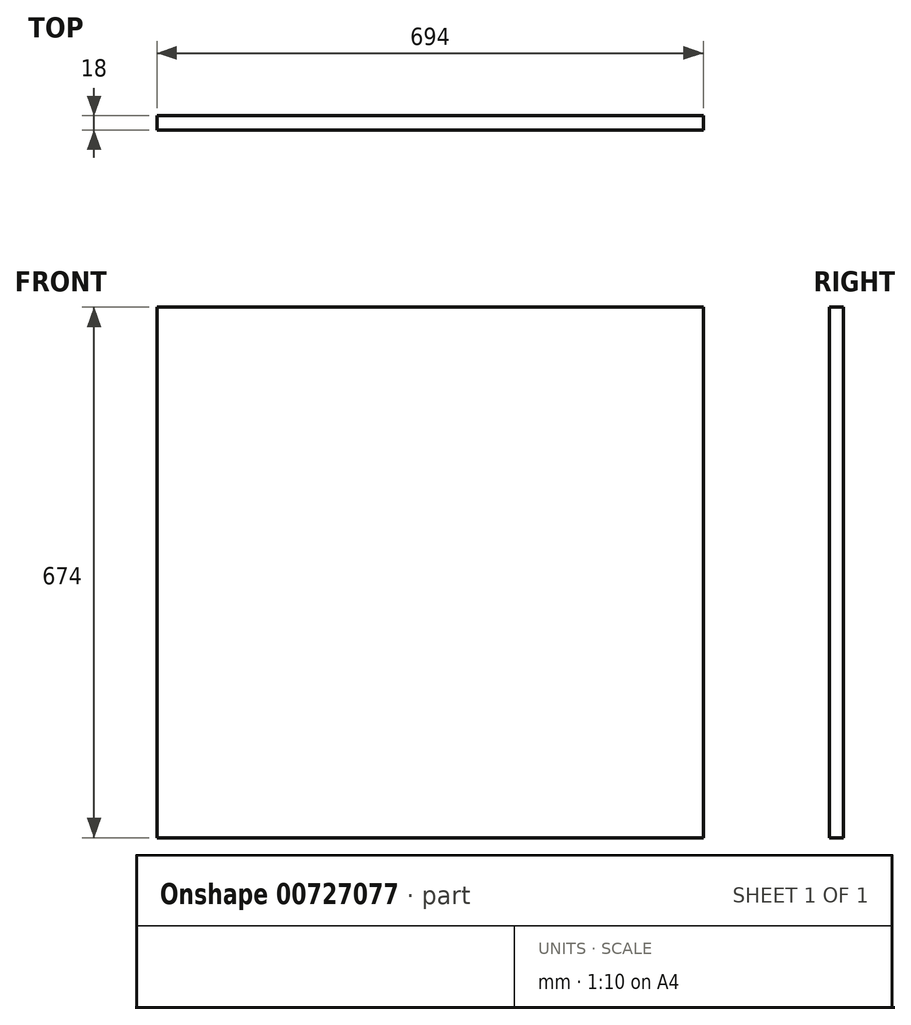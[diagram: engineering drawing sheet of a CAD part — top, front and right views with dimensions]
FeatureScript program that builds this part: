
annotation { "Feature Type Name" : "Feature", "Feature Type Description" : "" }
export const myFeature = defineFeature(function(context is Context, id is Id, definition is map)
    precondition{}
    {
        {
            var Q0;
            Q0=qCreatedBy(makeId("Front.planeOp"),FACE);
            var sketch = newSketch(context, id + "F0", { "sketchPlane" : qUnion([Q0])});
            skLineSegment(sketch, "E0.bottom", {"start": v(-347, 337) * mm, "end": v(347, 337) * mm});
            skLineSegment(sketch, "E0.top", {"start": v(-347, -337) * mm, "end": v(347, -337) * mm});
            skLineSegment(sketch, "E0.left", {"start": v(-347, 337) * mm, "end": v(-347, -337) * mm});
            skLineSegment(sketch, "E0.right", {"start": v(347, 337) * mm, "end": v(347, -337) * mm});
            skLineSegment(sketch, "E1", {"start": v(-347, 337) * mm, "end": v(347, -337) * mm, "construction": true});
            skLineSegment(sketch, "E2", {"start": v(347, 337) * mm, "end": v(-347, -337) * mm, "construction": true});
            skSolve(sketch);
        }
        {
            var Q0;
            Q0=qSketchRegion(id+"F0",true);
            extrude(context, id + "F1", {"entities" : qUnion([Q0]), "depth" : 18 * mm, "offsetDistance" : 25 * mm});
        }
    });
